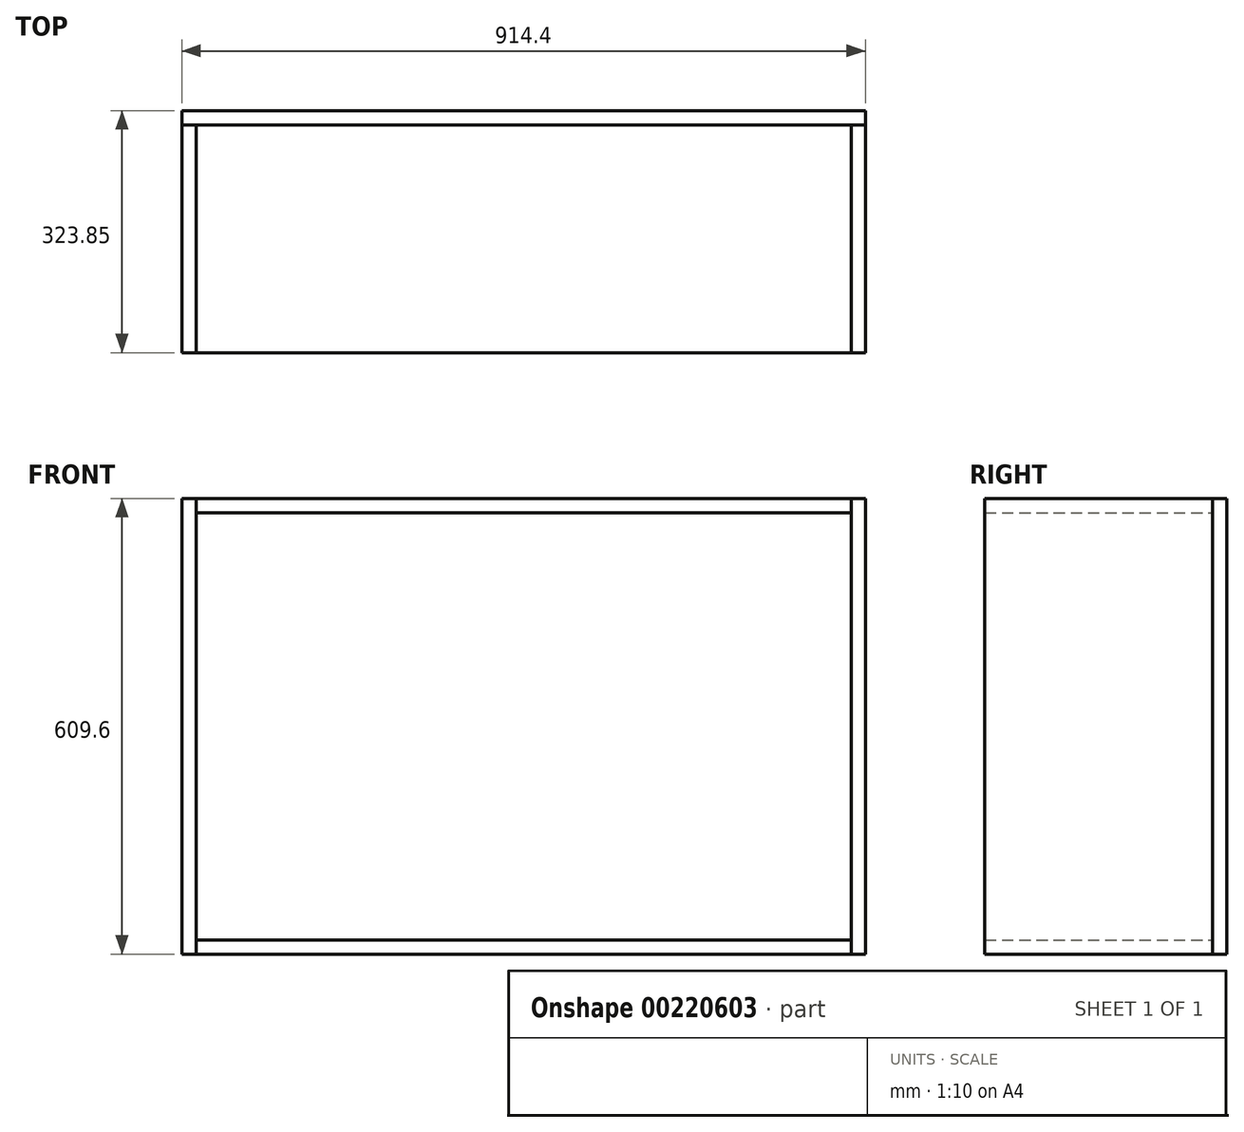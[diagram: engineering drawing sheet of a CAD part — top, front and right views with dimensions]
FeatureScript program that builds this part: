
annotation { "Feature Type Name" : "Feature", "Feature Type Description" : "" }
export const myFeature = defineFeature(function(context is Context, id is Id, definition is map)
    precondition{}
    {
        {
            var Q0;
            Q0=qCreatedBy(makeId("Front.planeOp"),FACE);
            var sketch = newSketch(context, id + "F0", { "sketchPlane" : qUnion([Q0])});
            skLineSegment(sketch, "E0.bottom", {"start": v(457.2, 304.8) * mm, "end": v(-457.2, 304.8) * mm});
            skLineSegment(sketch, "E0.top", {"start": v(457.2, -304.8) * mm, "end": v(-457.2, -304.8) * mm});
            skLineSegment(sketch, "E0.left", {"start": v(457.2, 304.8) * mm, "end": v(457.2, -304.8) * mm});
            skLineSegment(sketch, "E0.right", {"start": v(-457.2, 304.8) * mm, "end": v(-457.2, -304.8) * mm});
            skPoint(sketch, "E0.middle", {"position": v(0, 0) * mm});
            skSolve(sketch);
        }
        {
            var Q0;
            Q0=makeQuery(id+"F0.imprint","IMPRINT",FACE,{"disambiguationData":[TD([[makeQuery(id+"F0.imprint","IMPRINT",EDGE,{"derivedFrom":sQuery(id+"F0.wireOp",EDGE,"E0.bottom")}),1.0]])]});
            extrude(context, id + "F1", {"entities" : qUnion([Q0]), "depth" : 19.05 * mm});
        }
        {
            var Q0;
            Q0=makeQuery(id+"F1.opExtrude","CAP_FACE",FACE,{"disambiguationData":[OSD([sQuery(id+"F0.wireOp",EDGE,"E0.bottom"),sQuery(id+"F0.wireOp",EDGE,"E0.top"),sQuery(id+"F0.wireOp",EDGE,"E0.left"),sQuery(id+"F0.wireOp",EDGE,"E0.right")])],"isStart":false});
            var sketch = newSketch(context, id + "F2", { "sketchPlane" : qUnion([Q0])});
            skLineSegment(sketch, "E1.0.0", {"start": v(-457.2, -304.8) * mm, "end": v(457.2, -304.8) * mm});
            skLineSegment(sketch, "E1.0.1", {"start": v(457.2, -304.8) * mm, "end": v(457.2, 304.8) * mm});
            skLineSegment(sketch, "E1.0.2", {"start": v(457.2, 304.8) * mm, "end": v(-457.2, 304.8) * mm});
            skLineSegment(sketch, "E1.0.3", {"start": v(-457.2, 304.8) * mm, "end": v(-457.2, -304.8) * mm});
            skLineSegment(sketch, "E2.0", {"start": v(-438.15, -285.75) * mm, "end": v(438.15, -285.75) * mm});
            skLineSegment(sketch, "E2.1", {"start": v(-438.15, 304.8) * mm, "end": v(-438.15, -304.8) * mm});
            skLineSegment(sketch, "E2.2", {"start": v(438.15, 285.75) * mm, "end": v(-438.15, 285.75) * mm});
            skLineSegment(sketch, "E2.3", {"start": v(438.15, -304.8) * mm, "end": v(438.15, 304.8) * mm});
            skSolve(sketch);
        }
        {
            var Q0;
            {var subQ0=sQuery(id+"F2.wireOp",EDGE,"E1.0.3");Q0=makeQuery(id+"F2.imprint","IMPRINT",FACE,{"disambiguationData":[TD([[makeQuery(id+"F2.imprint","IMPRINT",EDGE,{"derivedFrom":subQ0}),1.0]])]});}
            extrude(context, id + "F3", {"entities" : qUnion([Q0]), "depth" : 304.8 * mm});
        }
        {
            var Q0;
            {var subQ5=sQuery(id+"F2.wireOp",EDGE,"E2.0");Q0=makeQuery(id+"F2.imprint","IMPRINT",FACE,{"disambiguationData":[TD([[makeQuery(id+"F2.imprint","IMPRINT",EDGE,{"derivedFrom":subQ5}),-1.0]])]});}
            var Q1;
            Q1=makeQuery(id+"F3.opExtrude","CAP_VERTEX",VERTEX,{"disambiguationData":[OSD([sQuery(id+"F2.wireOp",EDGE,"E1.0.0"),sQuery(id+"F2.wireOp",EDGE,"E2.1")])],"isStart":false});
            extrude(context, id + "F4", {"entities" : qUnion([Q0]), "endBound" : BoundingType.UP_TO_VERTEX, "endBoundEntityVertex" : qUnion([Q1]), "depth" : 25.4 * mm});
        }
        {
            var Q0;
            {var subQ5=sQuery(id+"F2.wireOp",EDGE,"E2.2");Q0=makeQuery(id+"F2.imprint","IMPRINT",FACE,{"disambiguationData":[TD([[makeQuery(id+"F2.imprint","IMPRINT",EDGE,{"derivedFrom":subQ5}),-1.0]])]});}
            var Q1;
            Q1=makeQuery(id+"F3.opExtrude","CAP_VERTEX",VERTEX,{"disambiguationData":[OSD([sQuery(id+"F2.wireOp",EDGE,"E1.0.2"),sQuery(id+"F2.wireOp",EDGE,"E2.1")])],"isStart":false});
            extrude(context, id + "F5", {"entities" : qUnion([Q0]), "endBound" : BoundingType.UP_TO_VERTEX, "endBoundEntityVertex" : qUnion([Q1]), "depth" : 25.4 * mm});
        }
        {
            var Q0;
            {var subQ5=sQuery(id+"F2.wireOp",EDGE,"E1.0.1");Q0=makeQuery(id+"F2.imprint","IMPRINT",FACE,{"disambiguationData":[TD([[makeQuery(id+"F2.imprint","IMPRINT",EDGE,{"derivedFrom":subQ5}),-1.0]])]});}
            var Q1;
            Q1=makeQuery(id+"F5.opExtrude","CAP_VERTEX",VERTEX,{"disambiguationData":[OSD([sQuery(id+"F2.wireOp",EDGE,"E2.2"),sQuery(id+"F2.wireOp",EDGE,"E2.3"),dummyQuery(id+"F5.vertexPlane.planeOp",FACE)])],"isStart":false});
            extrude(context, id + "F6", {"entities" : qUnion([Q0]), "endBound" : BoundingType.UP_TO_VERTEX, "endBoundEntityVertex" : qUnion([Q1]), "depth" : 25.4 * mm});
        }
    });
